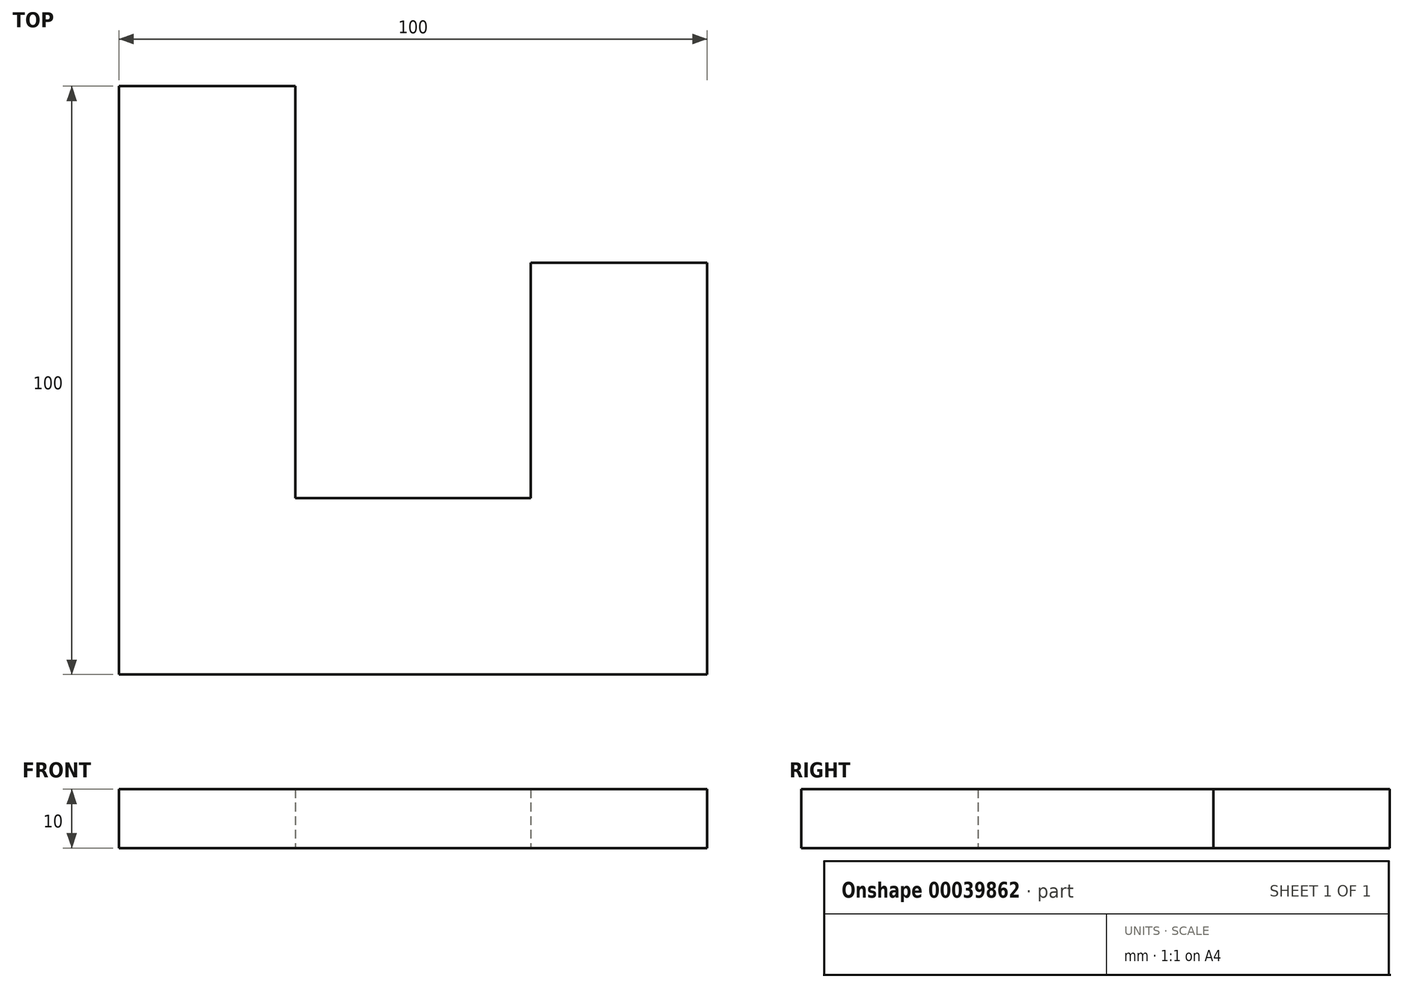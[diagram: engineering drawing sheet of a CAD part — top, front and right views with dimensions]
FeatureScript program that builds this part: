
annotation { "Feature Type Name" : "Feature", "Feature Type Description" : "" }
export const myFeature = defineFeature(function(context is Context, id is Id, definition is map)
    precondition{}
    {
        {
            var Q0;
            Q0=qCreatedBy(makeId("Top.planeOp"),FACE);
            var sketch = newSketch(context, id + "F0", { "sketchPlane" : qUnion([Q0])});
            skLineSegment(sketch, "E0.bottom", {"start": v(10.28, 24.03) * mm, "end": v(40.28, 24.03) * mm});
            skLineSegment(sketch, "E0.top", {"start": v(10.28, -45.97) * mm, "end": v(40.28, -45.97) * mm});
            skLineSegment(sketch, "E0.left", {"start": v(10.28, 24.03) * mm, "end": v(10.28, -45.97) * mm});
            skLineSegment(sketch, "E0.right", {"start": v(40.28, 24.03) * mm, "end": v(40.28, -45.97) * mm});
            skLineSegment(sketch, "E1.bottom", {"start": v(10.28, -15.97) * mm, "end": v(-29.72, -15.97) * mm});
            skLineSegment(sketch, "E1.left", {"start": v(10.28, -15.97) * mm, "end": v(10.28, -42.01) * mm});
            skLineSegment(sketch, "E2.top", {"start": v(-29.72, 54.03) * mm, "end": v(-59.72, 54.03) * mm});
            skLineSegment(sketch, "E2.left", {"start": v(-29.72, -15.97) * mm, "end": v(-29.72, 54.03) * mm});
            skLineSegment(sketch, "E2.right", {"start": v(-59.72, -45.97) * mm, "end": v(-59.72, 54.03) * mm});
            skLineSegment(sketch, "E3", {"start": v(-29.72, -15.97) * mm, "end": v(-59.72, -15.97) * mm});
            skLineSegment(sketch, "E4", {"start": v(-59.72, -45.97) * mm, "end": v(10.28, -45.97) * mm});
            skLineSegment(sketch, "E5", {"start": v(-59.72, -15.97) * mm, "end": v(-59.72, -45.97) * mm});
            skSolve(sketch);
        }
        {
            var Q0;
            Q0=makeQuery(id+"F0.imprint","IMPRINT",FACE,{"disambiguationData":[TD([[makeQuery(id+"F0.imprint","IMPRINT",EDGE,{"derivedFrom":sQuery(id+"F0.wireOp",EDGE,"E2.top")}),1.0]])]});
            var Q1;
            Q1=makeQuery(id+"F0.imprint","IMPRINT",FACE,{"disambiguationData":[TD([[makeQuery(id+"F0.imprint","IMPRINT",EDGE,{"derivedFrom":sQuery(id+"F0.wireOp",EDGE,"E1.bottom")}),1.0]])]});
            var Q2;
            {var subQ1=sQuery(id+"F0.wireOp",EDGE,"E0.bottom");Q2=makeQuery(id+"F0.imprint","IMPRINT",FACE,{"disambiguationData":[TD([[makeQuery(id+"F0.imprint","IMPRINT",EDGE,{"derivedFrom":subQ1}),-1.0]])]});}
            extrude(context, id + "F1", {"entities" : qUnion([Q0, Q1, Q2]), "depth" : 10 * mm});
        }
    });
